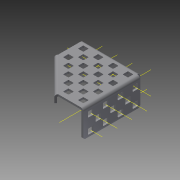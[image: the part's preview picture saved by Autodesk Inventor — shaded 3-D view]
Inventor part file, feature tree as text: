
AUTODESK INVENTOR PART (.ipt)
format: ipt  version: 2015 (Build 190159000, 159)  size: 662,016 bytes
history: native  units: in
note: dims shown in document units (in); Inventor stores cm internally (conversion verified against a paired STEP export)
features: other x69, pattern_linear x4, chamfer x1, imported_body x1
ambient origin geometry x8: Origin, YZ Plane, XZ Plane, XY Plane, X Axis, Y Axis, Z Axis, Center Point
bodies: Body1 (feature_tree)
feature tree (75):
  other  "Corner Gusset"
  chamfer  "Chamfer1"  Distance=1.5748in
  other  "right axis"
  other  "right inner axis"
  other  "back axis"
  other  "back inner axis"
  pattern_linear  "right axes"  Count1=3 Spacing1=0.5in
  pattern_linear  "right inner axes"  Count1=3 Spacing1=0.5in
  pattern_linear  "back axes"  Count1=4 Spacing1=0.5in
  pattern_linear  "back inner axes"  Count1=2 Spacing1=0.5in
  other  "Work Axis1"
  other  "Work Axis2"
  other  "Work Axis3"
  other  "Work Axis4"
  other  "Work Axis5"
  other  "Work Axis6"
  other  "Work Axis7"
  other  "Work Axis8"
  other  "Work Axis9"
  other  "Work Axis10"
  other  "Work Axis11"
  other  "Work Axis12"
  other  "Work Axis13"
  other  "Work Axis14"
  other  "Work Axis15"
  other  "Work Axis16"
  other  "Work Axis17"
  other  "Work Axis18"
  other  "Work Axis19"
  other  "Work Axis20"
  other  "Work Axis21"
  imported_body  "Base1"
  other  "Work Point1"
  other  "Work Point2"
  other  "Work Point3"
  other  "Work Point4"
  other  "Work Point5"
  other  "Work Point6"
  other  "Work Point7"
  other  "Work Point8"
  other  "Work Point9"
  other  "Work Point10"
  other  "Work Point11"
  other  "Work Point12"
  other  "Work Point13"
  other  "Work Point14"
  other  "Work Point15"
  other  "Work Point16"
  other  "Work Point17"
  other  "Work Point18"
  other  "Work Point19"
  other  "Work Point20"
  other  "Work Point21"
  other  "Work Point22"
  other  "Work Point23"
  other  "Work Point24"
  other  "Work Point25"
  other  "Work Axis26"
  other  "Work Axis27"
  other  "Work Axis28"
  other  "Work Axis29"
  other  "Work Axis30"
  other  "Work Axis31"
  other  "Work Axis32"
  other  "Work Axis33"
  other  "Work Axis34"
  other  "Work Axis35"
  other  "Work Axis36"
  other  "Work Axis37"
  other  "Work Axis38"
  other  "Work Axis39"
  other  "Work Axis40"
  other  "Work Axis41"
  other  "Work Axis42"
  other  "Work Axis43"
